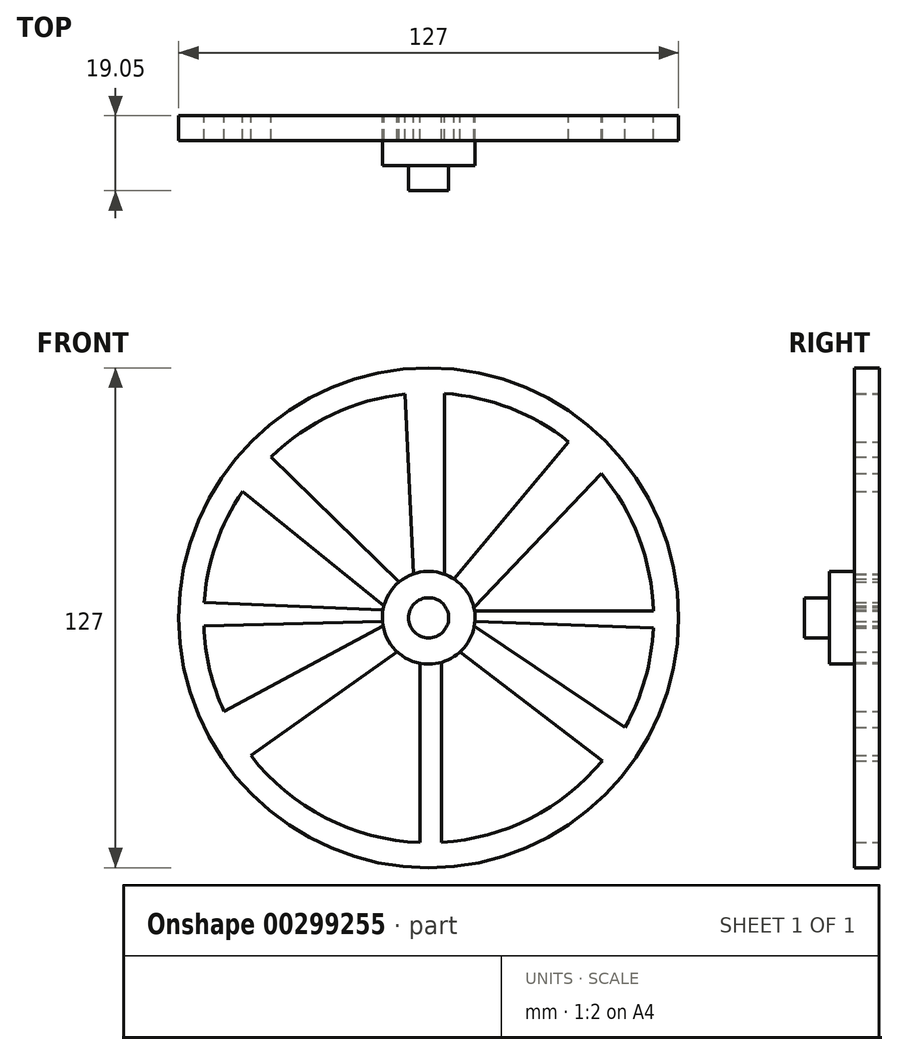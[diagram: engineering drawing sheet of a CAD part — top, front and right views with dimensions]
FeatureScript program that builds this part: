
annotation { "Feature Type Name" : "Feature", "Feature Type Description" : "" }
export const myFeature = defineFeature(function(context is Context, id is Id, definition is map)
    precondition{}
    {
        {
            var Q0;
            Q0=qCreatedBy(makeId("Front.planeOp"),FACE);
            var sketch = newSketch(context, id + "F0", { "sketchPlane" : qUnion([Q0])});
            skCircle(sketch, "E0", {"center": v(0, 0) * mm, "radius": 57.15 * mm});
            skCircle(sketch, "E1.0", {"center": v(0, 0) * mm, "radius": 63.5 * mm});
            skCircle(sketch, "E2", {"center": v(0, 0) * mm, "radius": 11.78 * mm});
            skCircle(sketch, "E3", {"center": v(0, 0) * mm, "radius": 5.1 * mm});
            skLineSegment(sketch, "E4", {"start": v(-47.29, 32.1) * mm, "end": v(-11.37, 3.07) * mm});
            skLineSegment(sketch, "E5", {"start": v(-40, 40.82) * mm, "end": v(-7.52, 9.06) * mm});
            skLineSegment(sketch, "E6", {"start": v(-6.06, 56.83) * mm, "end": v(-3.83, 11.14) * mm});
            skLineSegment(sketch, "E7", {"start": v(4.09, 57) * mm, "end": v(4.09, 11.05) * mm});
            skLineSegment(sketch, "E8", {"start": v(35.58, 44.73) * mm, "end": v(6.47, 9.84) * mm});
            skLineSegment(sketch, "E9", {"start": v(11.48, 2.62) * mm, "end": v(43.85, 36.65) * mm});
            skLineSegment(sketch, "E10", {"start": v(7.98, -8.66) * mm, "end": v(44.12, -36.33) * mm});
            skLineSegment(sketch, "E11", {"start": v(-2.19, -11.57) * mm, "end": v(-2.19, -57.1) * mm});
            skLineSegment(sketch, "E12", {"start": v(3.3, -11.3) * mm, "end": v(3.3, -57.06) * mm});
            skLineSegment(sketch, "E13", {"start": v(-11.59, -2.12) * mm, "end": v(-51.96, -23.79) * mm});
            skLineSegment(sketch, "E14", {"start": v(-7.99, -8.65) * mm, "end": v(-45.18, -35) * mm});
            skLineSegment(sketch, "E15", {"start": v(11.59, -2.12) * mm, "end": v(49.92, -27.81) * mm});
            skLineSegment(sketch, "E16", {"start": v(11.64, 1.78) * mm, "end": v(57.12, 1.78) * mm});
            skLineSegment(sketch, "E17", {"start": v(11.74, -0.91) * mm, "end": v(57.1, -2.54) * mm});
            skLineSegment(sketch, "E18", {"start": v(-11.62, 1.95) * mm, "end": v(-57.02, 3.85) * mm});
            skLineSegment(sketch, "E19", {"start": v(-57.11, -2.08) * mm, "end": v(-11.74, -0.93) * mm});
            skSolve(sketch);
        }
        {
            var Q0;
            Q0 = qSketchRegion(id + "F0", true);
            var Q1;
            {var subQ0=sQuery(id+"F0.wireOp",EDGE,"E4");Q1=makeQuery(id+"F0.imprint","IMPRINT",FACE,{"disambiguationData":[TD([[makeQuery(id+"F0.imprint","IMPRINT",EDGE,{"derivedFrom":subQ0}),1.0]])]});}
            var Q2;
            {var subQ0=sQuery(id+"F0.wireOp",EDGE,"E18");Q2=makeQuery(id+"F0.imprint","IMPRINT",FACE,{"disambiguationData":[TD([[makeQuery(id+"F0.imprint","IMPRINT",EDGE,{"derivedFrom":subQ0}),1.0]])]});}
            var Q3;
            {var subQ0=sQuery(id+"F0.wireOp",EDGE,"E13");Q3=makeQuery(id+"F0.imprint","IMPRINT",FACE,{"disambiguationData":[TD([[makeQuery(id+"F0.imprint","IMPRINT",EDGE,{"derivedFrom":subQ0}),1.0]])]});}
            var Q4;
            {var subQ0=sQuery(id+"F0.wireOp",EDGE,"E10");Q4=makeQuery(id+"F0.imprint","IMPRINT",FACE,{"disambiguationData":[TD([[makeQuery(id+"F0.imprint","IMPRINT",EDGE,{"derivedFrom":subQ0}),1.0]])]});}
            var Q5;
            {var subQ0=sQuery(id+"F0.wireOp",EDGE,"E8");Q5=makeQuery(id+"F0.imprint","IMPRINT",FACE,{"disambiguationData":[TD([[makeQuery(id+"F0.imprint","IMPRINT",EDGE,{"derivedFrom":subQ0}),1.0]])]});}
            var Q6;
            {var subQ0=sQuery(id+"F0.wireOp",EDGE,"E6");Q6=makeQuery(id+"F0.imprint","IMPRINT",FACE,{"disambiguationData":[TD([[makeQuery(id+"F0.imprint","IMPRINT",EDGE,{"derivedFrom":subQ0}),1.0]])]});}
            var Q7;
            {var subQ0=sQuery(id+"F0.wireOp",EDGE,"E16");Q7=makeQuery(id+"F0.imprint","IMPRINT",FACE,{"disambiguationData":[TD([[makeQuery(id+"F0.imprint","IMPRINT",EDGE,{"derivedFrom":subQ0}),-1.0]])]});}
            var Q8;
            {var subQ0=sQuery(id+"F0.wireOp",EDGE,"E11");Q8=makeQuery(id+"F0.imprint","IMPRINT",FACE,{"disambiguationData":[TD([[makeQuery(id+"F0.imprint","IMPRINT",EDGE,{"derivedFrom":subQ0}),1.0]])]});}
            extrude(context, id + "F1", {"entities" : qUnion([Q0, Q1, Q2, Q3, Q4, Q5, Q6, Q7, Q8]), "depth" : 6.35 * mm});
        }
        {
            var Q0;
            Q0=makeQuery(id+"F0.imprint","IMPRINT",FACE,{"disambiguationData":[TD([[makeQuery(id+"F0.imprint","IMPRINT",EDGE,{"derivedFrom":sQuery(id+"F0.wireOp",EDGE,"E3")}),-1.0]])]});
            extrude(context, id + "F2", {"entities" : qUnion([Q0]), "operationType" : NewBodyOperationType.ADD, "depth" : 12.7 * mm});
        }
        {
            var Q0;
            Q0=makeQuery(id+"F0.imprint","IMPRINT",FACE,{"disambiguationData":[TD([[makeQuery(id+"F0.imprint","IMPRINT",EDGE,{"derivedFrom":sQuery(id+"F0.wireOp",EDGE,"E3")}),1.0]])]});
            extrude(context, id + "F3", {"entities" : qUnion([Q0]), "operationType" : NewBodyOperationType.ADD, "depth" : 19.05 * mm});
        }
    });
